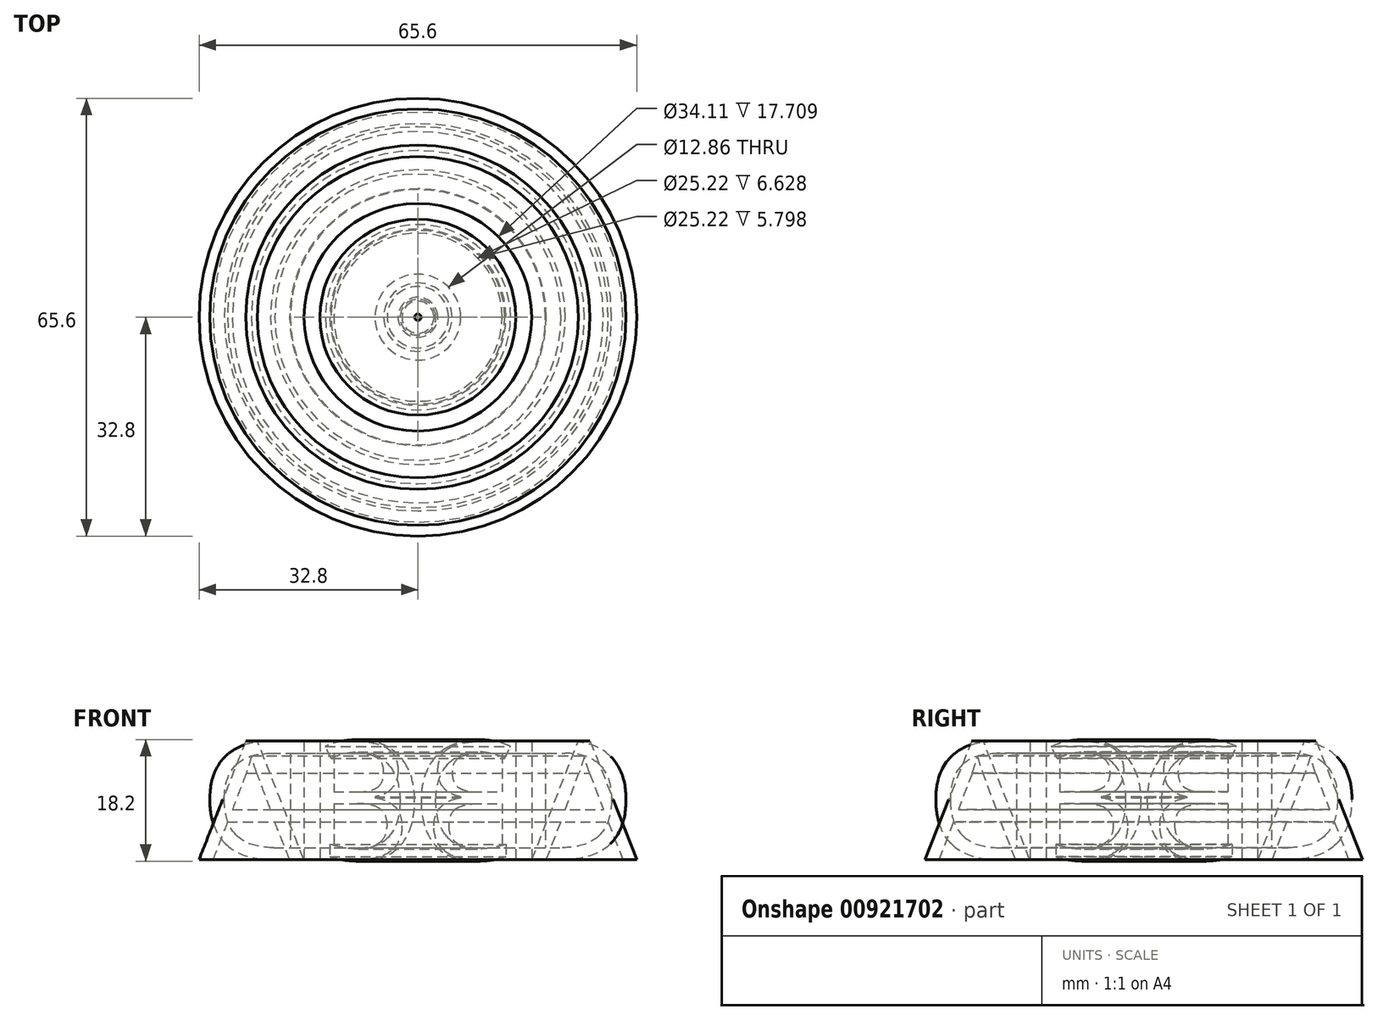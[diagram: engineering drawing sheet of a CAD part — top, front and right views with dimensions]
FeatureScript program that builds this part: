
annotation { "Feature Type Name" : "Feature", "Feature Type Description" : "" }
export const myFeature = defineFeature(function(context is Context, id is Id, definition is map)
    precondition{}
    {
        {
            var Q0;
            Q0=qCreatedBy(makeId("Front.planeOp"),FACE);
            var sketch = newSketch(context, id + "F0", { "sketchPlane" : qUnion([Q0])});
            skText(sketch, "E0", { "text": "ABCD\n", "fontName": "OpenSans-Regular.ttf"});
            const initialGuessF0  = {"E0": [0, -0.01786, 1, 0, 0.01786]};
            skSetInitialGuess(sketch, initialGuessF0);
            skSolve(sketch);
        }
        {
            var Q0;
            Q0 = qSketchRegion(id + "F0", true);
            var Q1;
            Q1=sQuery(id+"F0.wireOp",EDGE,"E0.sketch_text.center");
            revolve(context, id + "F1", {"surfaceOperationType" : NewSurfaceOperationType.NEW, "entities" : qUnion([Q0]), "axis" : qUnion([Q1]), "revolveType" : RevolveType.FULL});
        }
    });
